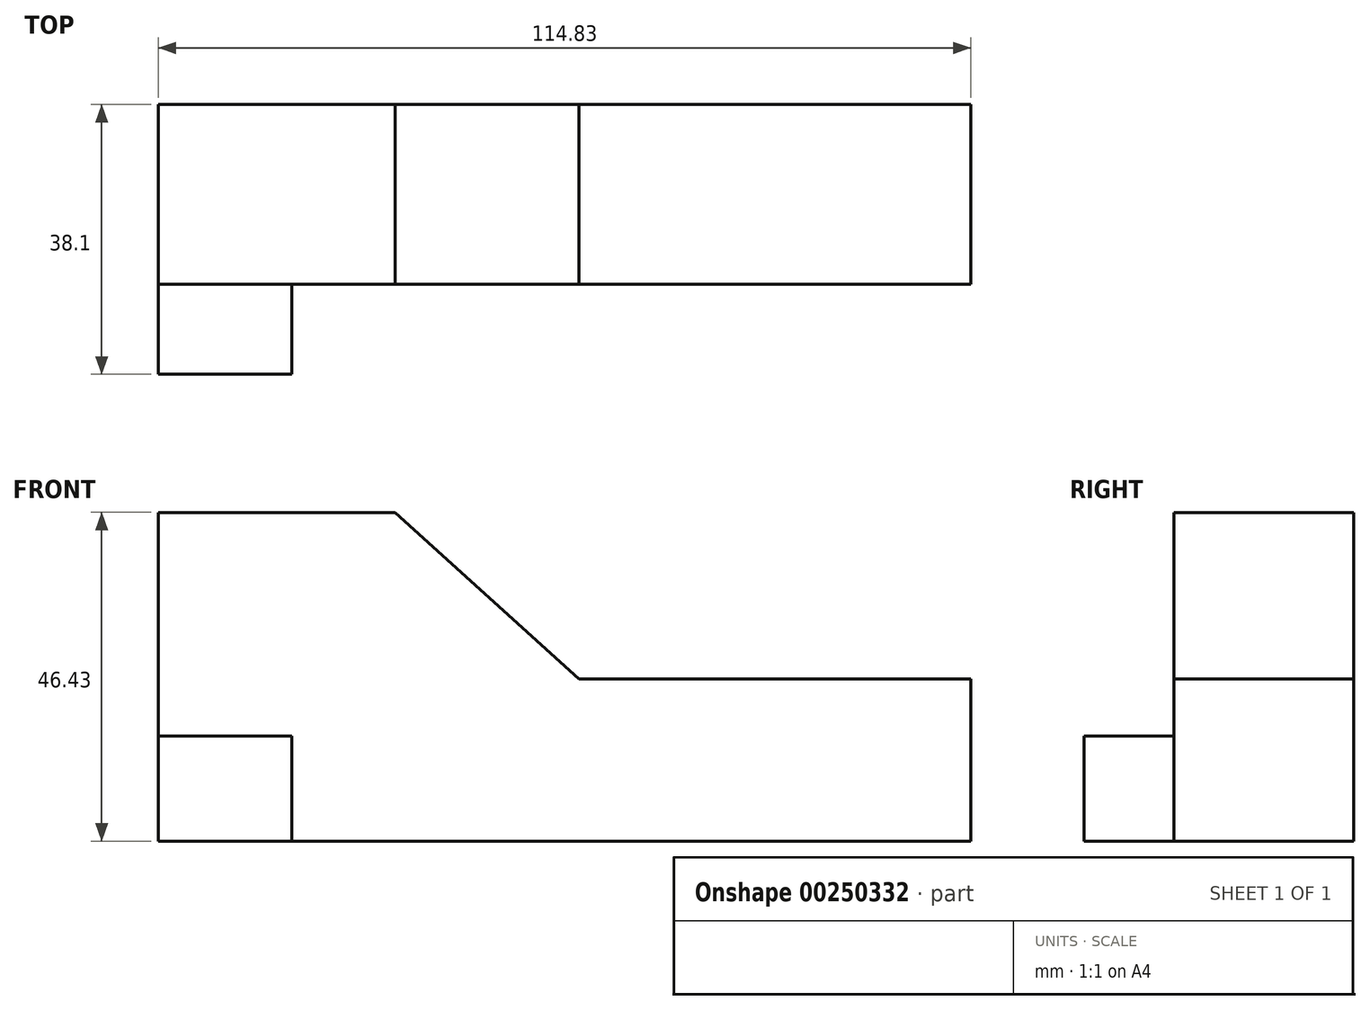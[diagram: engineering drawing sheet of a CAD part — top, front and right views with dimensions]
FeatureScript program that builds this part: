
annotation { "Feature Type Name" : "Feature", "Feature Type Description" : "" }
export const myFeature = defineFeature(function(context is Context, id is Id, definition is map)
    precondition{}
    {
        {
            var Q0;
            Q0=qCreatedBy(makeId("Front.planeOp"),FACE);
            var sketch = newSketch(context, id + "F0", { "sketchPlane" : qUnion([Q0])});
            skLineSegment(sketch, "E0", {"start": v(-61.28, 49.06) * mm, "end": v(-26, 49.06) * mm});
            skLineSegment(sketch, "E1", {"start": v(-26, 49.06) * mm, "end": v(0, 25.54) * mm});
            skLineSegment(sketch, "E2", {"start": v(0, 25.54) * mm, "end": v(55.4, 25.54) * mm});
            skLineSegment(sketch, "E3", {"start": v(55.4, 25.54) * mm, "end": v(55.4, 2.63) * mm});
            skPoint(sketch, "E4.end.orphan", {"position": v(0, 2.63) * mm});
            skLineSegment(sketch, "E5", {"start": v(55.4, 2.63) * mm, "end": v(-59.43, 2.63) * mm});
            skLineSegment(sketch, "E6", {"start": v(-59.43, 2.63) * mm, "end": v(-59.43, 49.06) * mm});
            skSolve(sketch);
        }
        {
            var Q0;
            {var subQ0=sQuery(id+"F0.wireOp",EDGE,"E1");Q0=makeQuery(id+"F0.imprint","IMPRINT",FACE,{"disambiguationData":[TD([[makeQuery(id+"F0.imprint","IMPRINT",EDGE,{"derivedFrom":subQ0}),-1.0]])]});}
            extrude(context, id + "F1", {"entities" : qUnion([Q0]), "depth" : 25.4 * mm});
        }
        {
            var Q0;
            Q0=makeQuery(id+"F1.opExtrude","CAP_FACE",FACE,{"disambiguationData":[OSD([sQuery(id+"F0.wireOp",EDGE,"E0"),sQuery(id+"F0.wireOp",EDGE,"E1"),sQuery(id+"F0.wireOp",EDGE,"E2"),sQuery(id+"F0.wireOp",EDGE,"E3"),sQuery(id+"F0.wireOp",EDGE,"E5"),sQuery(id+"F0.wireOp",EDGE,"E6")])],"isStart":false});
            var sketch = newSketch(context, id + "F2", { "sketchPlane" : qUnion([Q0])});
            skLineSegment(sketch, "E7", {"start": v(-59.43, 17.49) * mm, "end": v(-40.55, 17.49) * mm});
            skLineSegment(sketch, "E8", {"start": v(-40.55, 17.49) * mm, "end": v(-40.55, 2.63) * mm});
            skLineSegment(sketch, "E9", {"start": v(-40.55, 2.63) * mm, "end": v(-59.43, 2.63) * mm});
            skLineSegment(sketch, "E10", {"start": v(-59.43, 2.63) * mm, "end": v(-59.43, 17.49) * mm});
            skSolve(sketch);
        }
        {
            var Q0;
            Q0=makeQuery(id+"F2.imprint","IMPRINT",FACE,{"disambiguationData":[TD([[makeQuery(id+"F2.imprint","IMPRINT",EDGE,{"derivedFrom":sQuery(id+"F2.wireOp",EDGE,"E7")}),-1.0]])]});
            extrude(context, id + "F3", {"entities" : qUnion([Q0]), "operationType" : NewBodyOperationType.ADD, "depth" : 12.7 * mm});
        }
    });
